# Revit family: MIREFA-EDL-1X3xWSxMRMx
name_source: partatom
category: Leuchten
units: mm (PartAtom-declared; Revit-internal decimal feet)

## family parameters
Basisbauteil = Fläche
Beim Laden mit Abzugskörper schneiden = Nein
Bemaßung runder Anschluss = Durchmesser verwenden
Gemeinsam genutzt = Nein
Lichtquelle = Ja
OmniClass-Nummer = 23.80.70.11
OmniClass-Titel = Luminaries for Internal Lighting
Raumberechnungspunkt = Nein
Teiletyp = Normal

## types (4) — shared parameters
Baugruppenkennzeichen = D5020200
Datei für fotometrisches Netz = MIREFA.IES
Emissionsform beim Rendern sichtbar = Nein
Farbfilter = 16777215
Farbtemperaturverschiebung bei Dämpfen der Lampe = <Keine Auswahl>
Hersteller = RIDI Leuchten GmbH
Lampe = LED
Neigungswinkel = 90.00°
Scheinlast = 10 VA
URL = https://www.spectral.de
Von Breite des Rechtecks ausssenden = 50 mm  [stored 0.164042 ft]
Von Länge des Rechtecks aussenden = 170 mm  [stored 0.557743 ft]
brand = Spectral
conformity mark = CE
electrical safety class = 1
height = 60 mm  [stored 0.19685 ft]
ingress protection (IP) code = IP20
length = 240 mm  [stored 0.787402 ft]
nominal frequency = 50-60Hz
nominal voltage = 230
rated input power = 10
voltage type (AC, DC, UC) = AC
weight = 0,6kg
width = 80 mm  [stored 0.262467 ft]
zero-valued in all types: Vorgabe-Ansicht

## per-type parameters (varying)
| type | Modell |
| MIREFA-EDL-1X3 DAFWS830MRM0125 | SPG0330325AH |
| MIREFA-EDL-1X3 DAFWS840MRM0125 | SPG0330326AH |
| MIREFA-EDL-1X3 NDFWS830MRM0125 | SPG0320325AH |
| MIREFA-EDL-1X3 NDFWS840MRM0125 | SPG0320326AH |

note: column(s) folded — value = type name in every type: product name

note: [stored X ft] marks values corroborated as IEEE doubles in the binary element streams (Revit-internal decimal feet)
